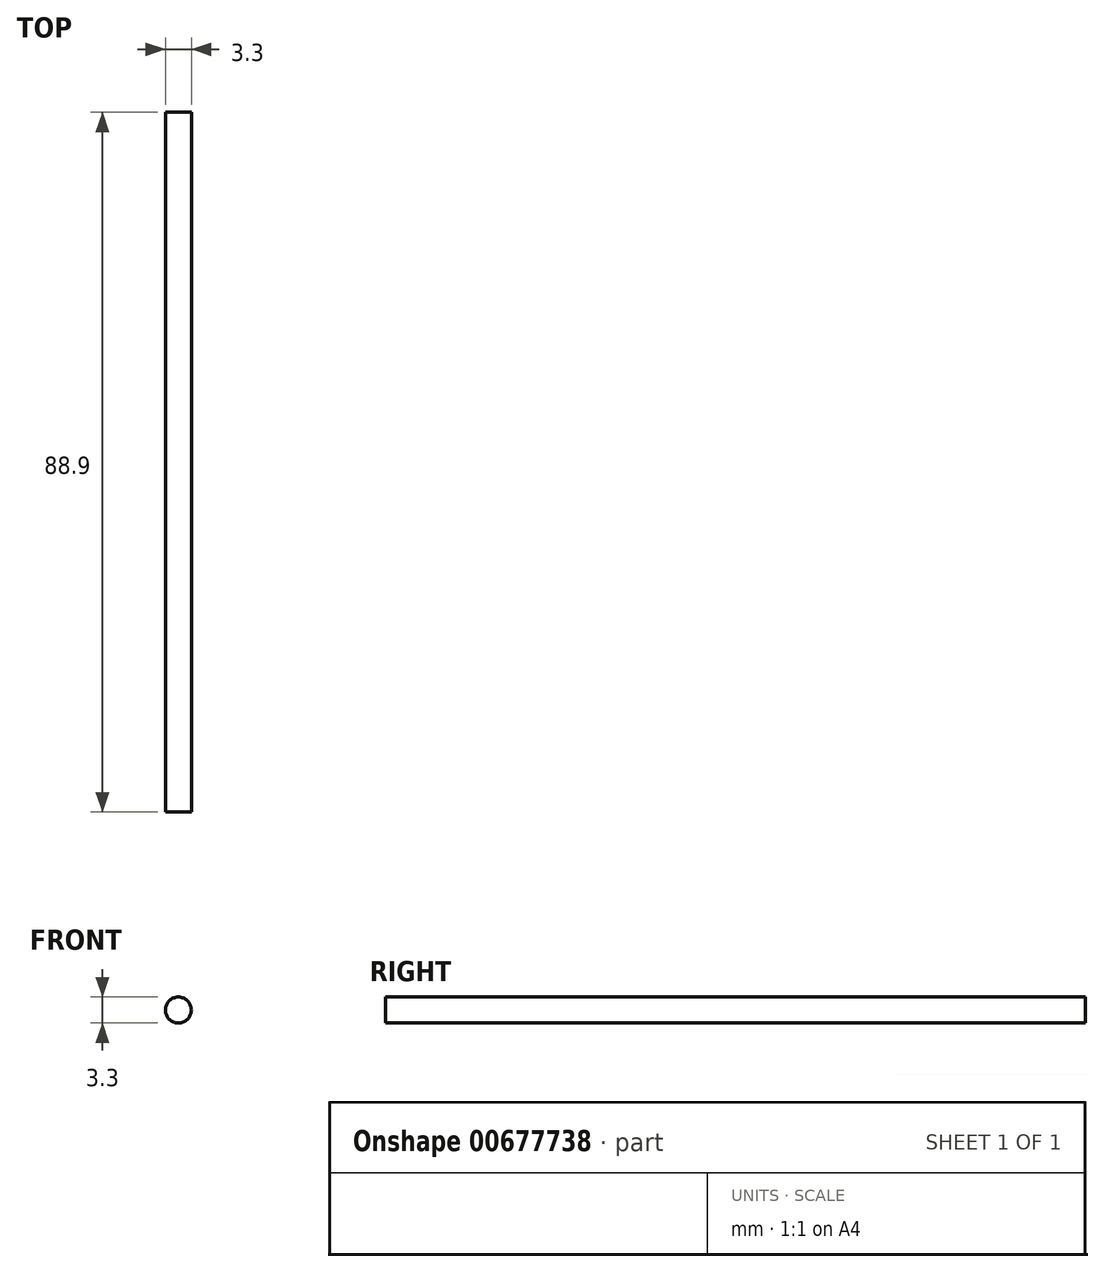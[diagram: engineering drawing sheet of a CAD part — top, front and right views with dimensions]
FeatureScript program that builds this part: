
annotation { "Feature Type Name" : "Feature", "Feature Type Description" : "" }
export const myFeature = defineFeature(function(context is Context, id is Id, definition is map)
    precondition{}
    {
        {
            var Q0;
            Q0=qCreatedBy(makeId("Front.planeOp"),FACE);
            var sketch = newSketch(context, id + "F0", { "sketchPlane" : qUnion([Q0])});
            skCircle(sketch, "E0", {"center": v(0, 0) * mm, "radius": 1.65 * mm});
            skLineSegment(sketch, "E1", {"start": v(0, -1.65) * mm, "end": v(0, 1.65) * mm});
            skLineSegment(sketch, "E2", {"start": v(0, 1.65) * mm, "end": v(0, -1.65) * mm});
            skSolve(sketch);
        }
        {
            var Q0;
            Q0=makeQuery(id+"F0.imprint","IMPRINT",FACE,{"disambiguationData":[TD([[makeQuery(id+"F0.imprint","IMPRINT",EDGE,{"derivedFrom":sQuery(id+"F0.wireOp",EDGE,"E0")}),1.0]])]});
            extrude(context, id + "F1", {"entities" : qUnion([Q0]), "oppositeDirection" : true, "depth" : 63.5 * mm, "offsetDistance" : 25.4 * mm});
        }
        {
            var Q0;
            Q0=makeQuery(id+"F1.opExtrude","CAP_FACE",FACE,{"disambiguationData":[OSD([sQuery(id+"F0.wireOp",EDGE,"E0")])],"isStart":true});
            extrude(context, id + "F2", {"entities" : qUnion([Q0]), "operationType" : NewBodyOperationType.ADD, "depth" : 25.4 * mm, "offsetDistance" : 25.4 * mm});
        }
    });
